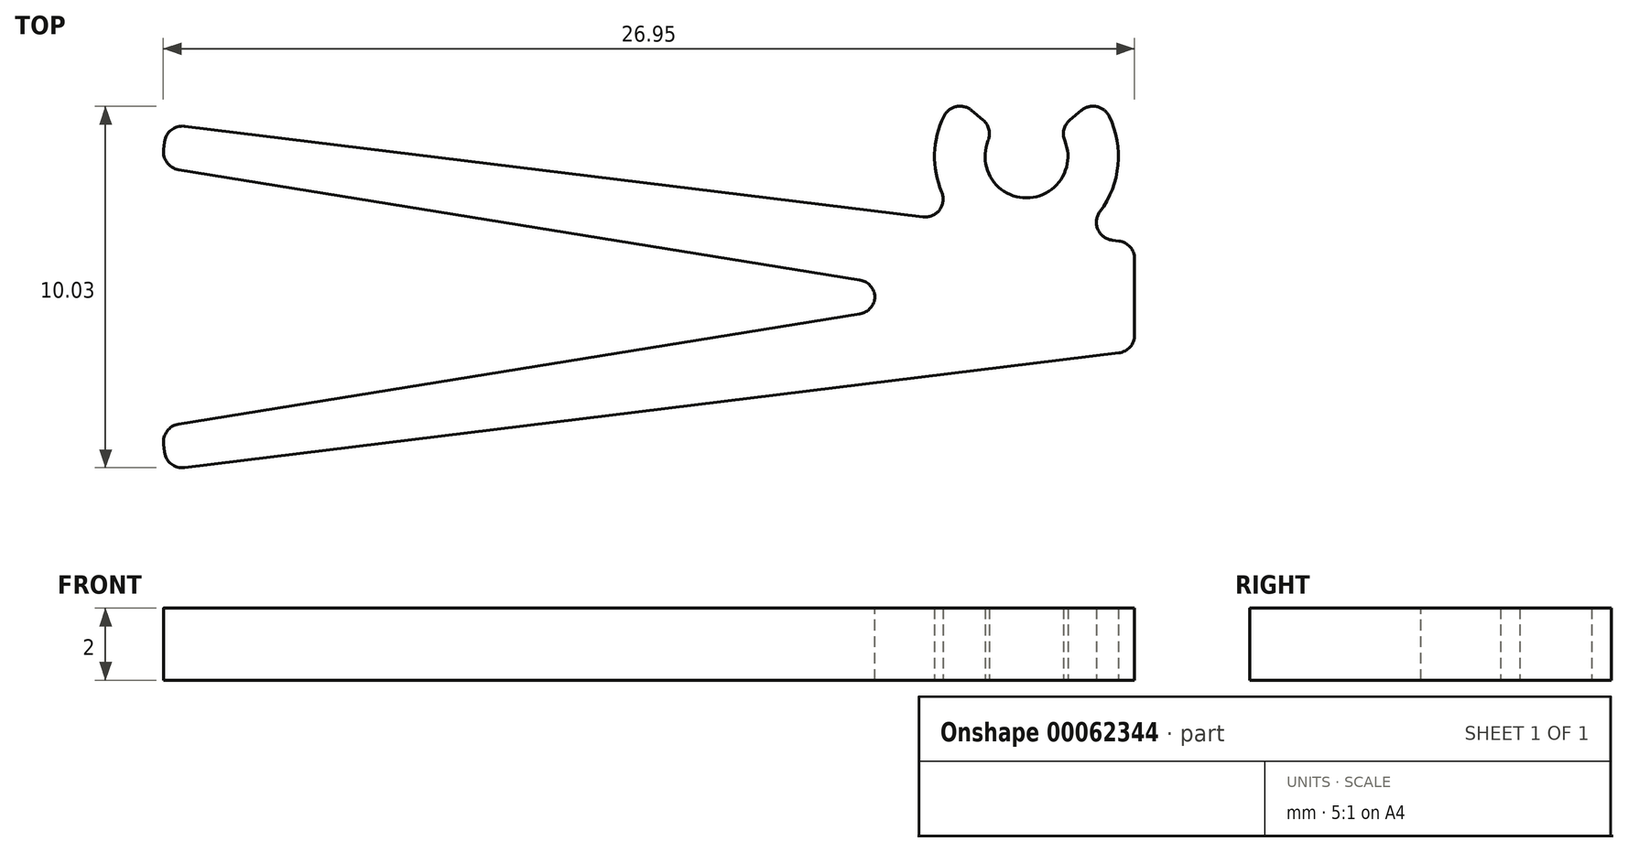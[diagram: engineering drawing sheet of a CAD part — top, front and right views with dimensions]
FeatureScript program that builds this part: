
annotation { "Feature Type Name" : "Feature", "Feature Type Description" : "" }
export const myFeature = defineFeature(function(context is Context, id is Id, definition is map)
    precondition{}
    {
        {
            var Q0;
            Q0=qCreatedBy(makeId("Top.planeOp"),FACE);
            var sketch = newSketch(context, id + "F0", { "sketchPlane" : qUnion([Q0])});
            skLineSegment(sketch, "E0", {"start": v(-19.65, -4.8) * mm, "end": v(-19.8, -3.6) * mm});
            skLineSegment(sketch, "E1", {"start": v(-19.65, -4.8) * mm, "end": v(7.2, -1.5) * mm});
            skLineSegment(sketch, "E2", {"start": v(7.2, 1.5) * mm, "end": v(7.2, -1.5) * mm});
            skLineSegment(sketch, "E3", {"start": v(7.2, 1.5) * mm, "end": v(5.5, 1.7) * mm});
            skPoint(sketch, "E4", {"position": v(7.2, 0) * mm});
            skLineSegment(sketch, "E5", {"start": v(-19.65, 4.8) * mm, "end": v(-19.8, 3.6) * mm});
            skLineSegment(sketch, "E6", {"start": v(-19.8, 3.6) * mm, "end": v(-19.8, -3.6) * mm, "construction": true});
            skPoint(sketch, "E7", {"position": v(-19.8, 0) * mm});
            skLineSegment(sketch, "E8", {"start": v(0, 0.4) * mm, "end": v(0, -0.4) * mm});
            skLineSegment(sketch, "E9", {"start": v(-19.8, 3.6) * mm, "end": v(0, 0.4) * mm});
            skLineSegment(sketch, "E10", {"start": v(0, -0.4) * mm, "end": v(-19.8, -3.6) * mm});
            skArc(sketch, "E11", {"start": v(2.25, 5.54) * mm, "mid": v(1.65, 3.78) * mm, "end": v(2.4, 2.09) * mm});
            skArc(sketch, "E12", {"start": v(3.32, 4.64) * mm, "mid": v(4.2, 2.75) * mm, "end": v(5.08, 4.64) * mm});
            skLineSegment(sketch, "E13", {"start": v(3.32, 4.64) * mm, "end": v(2.25, 5.54) * mm});
            skLineSegment(sketch, "E14", {"start": v(5.08, 4.64) * mm, "end": v(6.15, 5.54) * mm});
            skLineSegment(sketch, "E15", {"start": v(4.2, 3.9) * mm, "end": v(4.2, 9.68) * mm, "construction": true});
            skLineSegment(sketch, "E16", {"start": v(2.25, 5.54) * mm, "end": v(6.15, 5.54) * mm, "construction": true});
            skArc(sketch, "E17.trimOffspring", {"start": v(5.5, 1.7) * mm, "mid": v(6.71, 3.47) * mm, "end": v(6.15, 5.54) * mm});
            skLineSegment(sketch, "E18.trimOffspring", {"start": v(2.4, 2.09) * mm, "end": v(-19.65, 4.8) * mm});
            skSolve(sketch);
        }
        {
            var Q0;
            Q0 = qSketchRegion(id + "F0", true);
            extrude(context, id + "F1", {"entities" : qUnion([Q0]), "endBound" : BoundingType.SYMMETRIC, "depth" : 2 * mm});
        }
        {
            var Q0;
            Q0=makeQuery(id+"F1.opExtrude","SWEPT_EDGE",EDGE,{"disambiguationData":[OSD([sQuery(id+"F0.wireOp",EDGE,"E12"),sQuery(id+"F0.wireOp",EDGE,"E13")])]});
            var Q1;
            Q1=makeQuery(id+"F1.opExtrude","SWEPT_EDGE",EDGE,{"disambiguationData":[OSD([sQuery(id+"F0.wireOp",EDGE,"E11"),sQuery(id+"F0.wireOp",EDGE,"E13")])]});
            var Q2;
            Q2=makeQuery(id+"F1.opExtrude","SWEPT_EDGE",EDGE,{"disambiguationData":[OSD([sQuery(id+"F0.wireOp",EDGE,"E12"),sQuery(id+"F0.wireOp",EDGE,"E14")])]});
            var Q3;
            Q3=makeQuery(id+"F1.opExtrude","SWEPT_EDGE",EDGE,{"disambiguationData":[OSD([sQuery(id+"F0.wireOp",EDGE,"E14"),sQuery(id+"F0.wireOp",EDGE,"E17.trimOffspring")])]});
            var Q4;
            Q4=makeQuery(id+"F1.opExtrude","SWEPT_EDGE",EDGE,{"disambiguationData":[OSD([sQuery(id+"F0.wireOp",EDGE,"E2"),sQuery(id+"F0.wireOp",EDGE,"E3")])]});
            var Q5;
            Q5=makeQuery(id+"F1.opExtrude","SWEPT_EDGE",EDGE,{"disambiguationData":[OSD([sQuery(id+"F0.wireOp",EDGE,"E1"),sQuery(id+"F0.wireOp",EDGE,"E2")])]});
            var Q6;
            Q6=makeQuery(id+"F1.opExtrude","SWEPT_EDGE",EDGE,{"disambiguationData":[OSD([sQuery(id+"F0.wireOp",EDGE,"E8"),sQuery(id+"F0.wireOp",EDGE,"E10")])]});
            var Q7;
            Q7=makeQuery(id+"F1.opExtrude","SWEPT_EDGE",EDGE,{"disambiguationData":[OSD([sQuery(id+"F0.wireOp",EDGE,"E8"),sQuery(id+"F0.wireOp",EDGE,"E9")])]});
            var Q8;
            Q8=makeQuery(id+"F1.opExtrude","SWEPT_EDGE",EDGE,{"disambiguationData":[OSD([sQuery(id+"F0.wireOp",EDGE,"E0"),sQuery(id+"F0.wireOp",EDGE,"E10")])]});
            var Q9;
            Q9=makeQuery(id+"F1.opExtrude","SWEPT_EDGE",EDGE,{"disambiguationData":[OSD([sQuery(id+"F0.wireOp",EDGE,"E0"),sQuery(id+"F0.wireOp",EDGE,"E1")])]});
            var Q10;
            Q10=makeQuery(id+"F1.opExtrude","SWEPT_EDGE",EDGE,{"disambiguationData":[OSD([sQuery(id+"F0.wireOp",EDGE,"E5"),sQuery(id+"F0.wireOp",EDGE,"E9")])]});
            var Q11;
            Q11=makeQuery(id+"F1.opExtrude","SWEPT_EDGE",EDGE,{"disambiguationData":[OSD([sQuery(id+"F0.wireOp",EDGE,"E5"),sQuery(id+"F0.wireOp",EDGE,"E18.trimOffspring")])]});
            var Q12;
            Q12=makeQuery(id+"F1.opExtrude","SWEPT_EDGE",EDGE,{"disambiguationData":[OSD([sQuery(id+"F0.wireOp",EDGE,"E3"),sQuery(id+"F0.wireOp",EDGE,"E17.trimOffspring")])]});
            var Q13;
            Q13=makeQuery(id+"F1.opExtrude","SWEPT_EDGE",EDGE,{"disambiguationData":[OSD([sQuery(id+"F0.wireOp",EDGE,"E11"),sQuery(id+"F0.wireOp",EDGE,"E18.trimOffspring")])]});
            fillet(context, id + "F2", {"entities" : qUnion([Q0, Q1, Q2, Q3, Q4, Q5, Q6, Q7, Q8, Q9, Q10, Q11, Q12, Q13]), "radius" : 0.5 * mm, "tangentPropagation" : true, "allowEdgeOverflow" : false});
        }
    });
